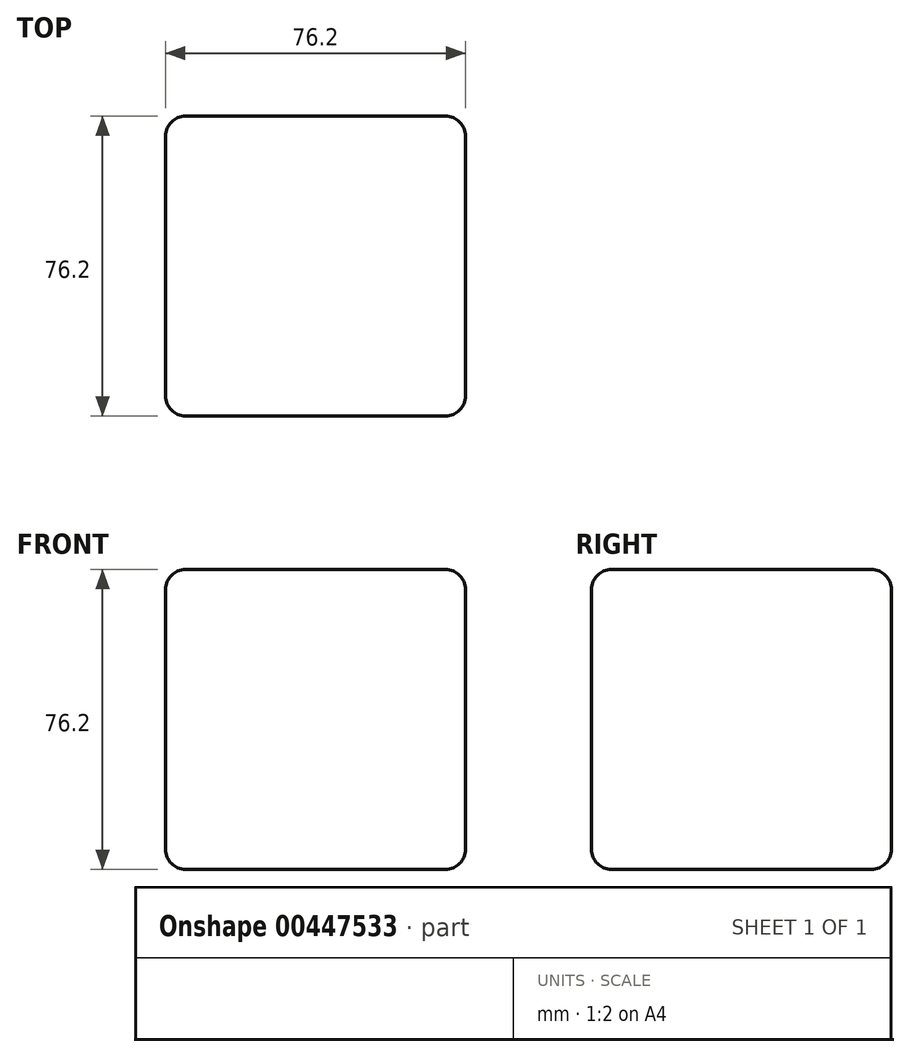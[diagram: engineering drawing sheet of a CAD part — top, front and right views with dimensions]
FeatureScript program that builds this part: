
annotation { "Feature Type Name" : "Feature", "Feature Type Description" : "" }
export const myFeature = defineFeature(function(context is Context, id is Id, definition is map)
    precondition{}
    {
        {
            var Q0;
            Q0=qCreatedBy(makeId("Front.planeOp"),FACE);
            var sketch = newSketch(context, id + "F0", { "sketchPlane" : qUnion([Q0])});
            skLineSegment(sketch, "E0.bottom", {"start": v(0, 0) * mm, "end": v(76.2, 0) * mm});
            skLineSegment(sketch, "E0.top", {"start": v(0, 76.2) * mm, "end": v(76.2, 76.2) * mm});
            skLineSegment(sketch, "E0.left", {"start": v(0, 0) * mm, "end": v(0, 76.2) * mm});
            skLineSegment(sketch, "E0.right", {"start": v(76.2, 0) * mm, "end": v(76.2, 76.2) * mm});
            skSolve(sketch);
        }
        {
            var Q0;
            Q0 = qSketchRegion(id + "F0", true);
            extrude(context, id + "F1", {"entities" : qUnion([Q0]), "endBound" : BoundingType.SYMMETRIC, "depth" : 76.2 * mm});
        }
        {
            var Q0;
            Q0=makeQuery(id+"F1.opExtrude","SWEPT_EDGE",EDGE,{"disambiguationData":[OSD([sQuery(id+"F0.wireOp",EDGE,"E0.top"),sQuery(id+"F0.wireOp",EDGE,"E0.right")])]});
            var Q1;
            Q1=makeQuery(id+"F1.opExtrude","CAP_EDGE",EDGE,{"disambiguationData":[OSD([sQuery(id+"F0.wireOp",EDGE,"E0.right")])],"isStart":false});
            var Q2;
            Q2=makeQuery(id+"F1.opExtrude","CAP_EDGE",EDGE,{"disambiguationData":[OSD([sQuery(id+"F0.wireOp",EDGE,"E0.top")])],"isStart":false});
            var Q3;
            Q3=makeQuery(id+"F1.opExtrude","CAP_EDGE",EDGE,{"disambiguationData":[OSD([sQuery(id+"F0.wireOp",EDGE,"E0.top")])],"isStart":true});
            var Q4;
            Q4=makeQuery(id+"F1.opExtrude","CAP_EDGE",EDGE,{"disambiguationData":[OSD([sQuery(id+"F0.wireOp",EDGE,"E0.left")])],"isStart":true});
            var Q5;
            Q5=makeQuery(id+"F1.opExtrude","SWEPT_EDGE",EDGE,{"disambiguationData":[OSD([sQuery(id+"F0.wireOp",EDGE,"E0.top"),sQuery(id+"F0.wireOp",EDGE,"E0.left")])]});
            var Q6;
            Q6=makeQuery(id+"F1.opExtrude","CAP_EDGE",EDGE,{"disambiguationData":[OSD([sQuery(id+"F0.wireOp",EDGE,"E0.bottom")])],"isStart":true});
            var Q7;
            Q7=makeQuery(id+"F1.opExtrude","SWEPT_EDGE",EDGE,{"disambiguationData":[OSD([sQuery(id+"F0.wireOp",EDGE,"E0.bottom"),sQuery(id+"F0.wireOp",EDGE,"E0.right")])]});
            var Q8;
            Q8=makeQuery(id+"F1.opExtrude","CAP_EDGE",EDGE,{"disambiguationData":[OSD([sQuery(id+"F0.wireOp",EDGE,"E0.right")])],"isStart":true});
            var Q9;
            Q9=makeQuery(id+"F1.opExtrude","SWEPT_FACE",FACE,{"disambiguationData":[OSD([sQuery(id+"F0.wireOp",EDGE,"E0.bottom")])]});
            var Q10;
            Q10=makeQuery(id+"F1.opExtrude","CAP_EDGE",EDGE,{"disambiguationData":[OSD([sQuery(id+"F0.wireOp",EDGE,"E0.left")])],"isStart":false});
            fillet(context, id + "F2", {"entities" : qUnion([Q0, Q1, Q2, Q3, Q4, Q5, Q6, Q7, Q8, Q9, Q10]), "radius" : 5.08 * mm, "tangentPropagation" : true, "allowEdgeOverflow" : false});
        }
    });
